# Revit family: Турникет тумбовый PERCo_TB01.9
name_source: partatom
category: Mechanical Equipment
units: mm (PartAtom-declared; Revit-internal decimal feet)

## family parameters
Always vertical = No
Classification = None
Cut with Voids When Loaded = No
Part Type = Normal
Room Calculation Point = No
Round Connector Dimension = Use Diameter
Shared = No
Work Plane-Based = No

## types (2) — shared parameters
Built-in reader = Multi-format, 2 pcs
Current = 6 A
Dimensions = 1170×750×1030
Electrical connection = 220 B
Full name = TBC-01.9A Electromechanical Box Tripod Turnstile with a Card Capture Reader and Automatic Anti-Panic Barrier Arms
IP Code = IP41
Manufacturer = PERCo
Material = Housing ─ high-quality stainless steel. Top cover ─ stainless steel or radio-transparent artificial stone. Barrier arms ─ stainless steel.
Maximum dimensions of ACS controller = max. 160×150×35 mm
Maximum dimensions of installed readers = not provided
Name = TBС-01.9A Box tripod turnstile
Number = 1
Operating temperature = from +1°С to +50°С
Passageway width = 560 mm
Plank length = 567 mm  [stored 1.86024 ft]
Rated power = 72 W
Throughput rate = 30 persons/min
URL = https://www.perco.com
Unit of measurement = pcs
Voltage = 12 V
Weight = max. 68 kg

## per-type parameters (varying)
| type | Card capture reader capacity | Card reader |
| ТВ01.9A without built-in card reader | not provided | No |
| ТВС01.9А with built-in card reader | 350 cards | Yes |

note: [stored X ft] marks values corroborated as IEEE doubles in the binary element streams (Revit-internal decimal feet)
